# Revit family: 0006162
name_source: partatom
category: Generic Models
revit_build: Autodesk Revit 2018 (Build: 20170223_1515(x64)
units: mm (PartAtom-declared; Revit-internal decimal feet)

## family parameters
Can host rebar = No
Cut with Voids When Loaded = No
Host = Face
OmniClass Number = 23.80.70.00
OmniClass Title = Lighting
Part Type = Normal
Room Calculation Point = No
Round Connector Dimension = Use Diameter
Shared = No

## types (1)
- 0006162 PIXO MINI SURFACE 490LM 927 MB WHT
    Assembly Code = D5020200
    Cost = 0 $
    Default Elevation = 1219 mm
    Description = Integrated LED spotlight, Textured White - RAL9016, simple and slick integral design with no driver box and without any visible screws, ideal for retail applications, die-cast aluminium body, passive cooling heatsink. Beam angle: 40°, color temperature: 2700K , total system power: 6.5W, total fixture output: 490 lm, LOR: 100%, colour rendering: Ra: 90 typical, IR/UV free light source without heat radiation, operating voltage: 220-240V / 50-60Hz, electronic driver, non-dimmable, low LED flickerering rate (6%-20%), power factor: >0.90, electrical protection: Class I, Surface mounting ceiling rose, ingress protection rating: IP20, suitable for internal environment only, horizontal rotation: 345°, vertical tilt: 90°, dimensions: Ø41.5x125, weight: 0.219kg.
    Length = 60 mm  [stored 0.19685 ft]
    Material_1_SYL = <By Category>
    Material_2_SYL = <By Category>
    Material_3_SYL = <By Category>
    Material_4_SYL = <By Category>
    Model = Pixo Mini SURFACE 490lm 927 MB WHITE
    Type Image = <None>
    URL = 0.5
    Width = 60 mm  [stored 0.19685 ft]

note: [stored X ft] marks values corroborated as IEEE doubles in the binary element streams (Revit-internal decimal feet)

## geometry (parser evidence)
native form markers: Sweep x9
no freeform markers — native parametric forms only
